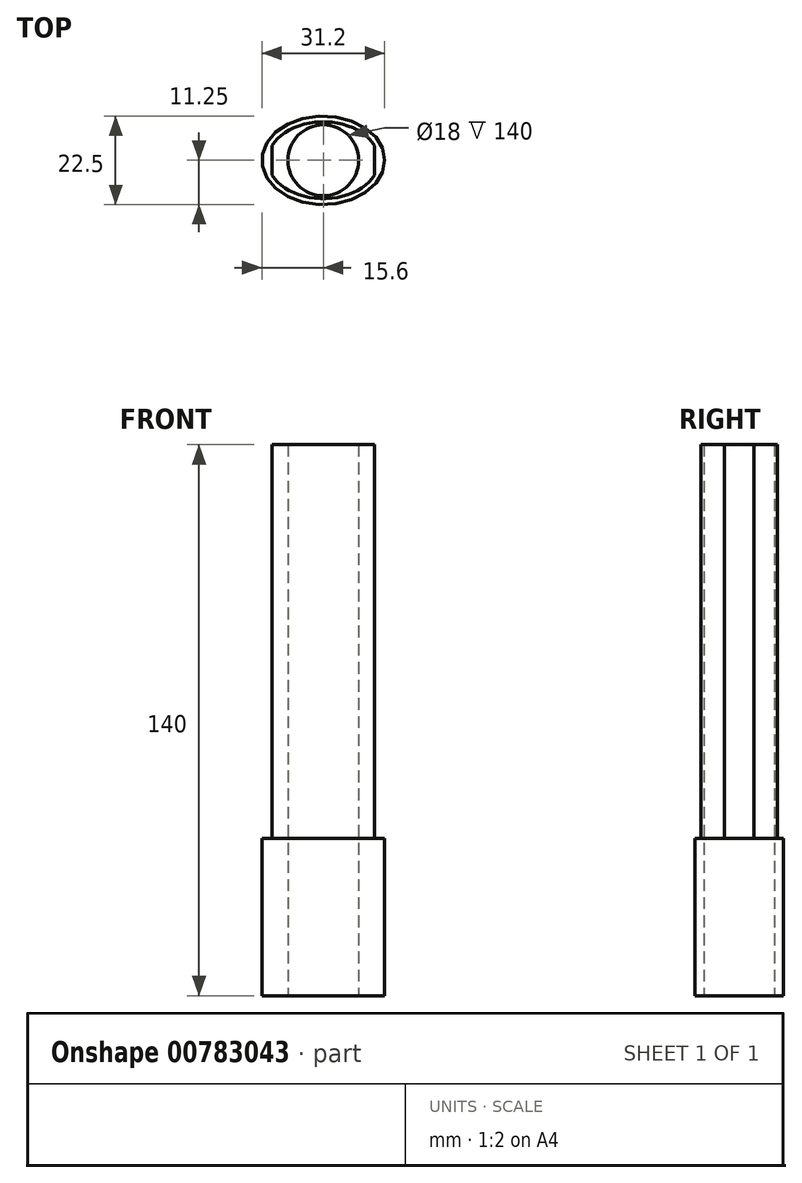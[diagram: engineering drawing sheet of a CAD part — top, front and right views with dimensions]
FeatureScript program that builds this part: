
annotation { "Feature Type Name" : "Feature", "Feature Type Description" : "" }
export const myFeature = defineFeature(function(context is Context, id is Id, definition is map)
    precondition{}
    {
        {
            var Q0;
            Q0=qCreatedBy(makeId("Top.planeOp"),FACE);
            var sketch = newSketch(context, id + "F0", { "sketchPlane" : qUnion([Q0])});
            skEllipse(sketch, "E0", {"center": v(0, 0) * mm, "majorRadius": 15.6 * mm, "minorRadius": 11.25 * mm, "majorAxis": v(1, 0)});
            skSolve(sketch);
        }
        {
            var Q0;
            Q0 = qSketchRegion(id + "F0", true);
            extrude(context, id + "F1", {"entities" : qUnion([Q0]), "depth" : 40 * mm, "offsetDistance" : 25.4 * mm});
        }
        {
            var Q0;
            Q0=makeQuery(id+"F1.opExtrude","CAP_FACE",FACE,{"disambiguationData":[OSD([sQuery(id+"F0.wireOp",EDGE,"E0")])],"isStart":false});
            var sketch = newSketch(context, id + "F2", { "sketchPlane" : qUnion([Q0])});
            skEllipticalArc(sketch, "E1", {});
            skLineSegment(sketch, "E2", {"start": v(13, 3.78) * mm, "end": v(13, -3.78) * mm});
            skLineSegment(sketch, "E3", {"start": v(-13, 3.78) * mm, "end": v(-13, -3.78) * mm});
            skEllipticalArc(sketch, "E4.trimOffspring", {});
            const initialGuessF2  = {"E1": [0, 0, 1, 0, 0.0141, 0.00975, 0.3976184106167527, 2.743974242973041], "E4.trimOffspring": [0, 0, 1, 0, 0.0141, 0.00975, 3.5392110642065457, 5.885566896562835]};
            skSetInitialGuess(sketch, initialGuessF2);
            skSolve(sketch);
        }
        {
            var Q0;
            Q0 = qSketchRegion(id + "F2", true);
            extrude(context, id + "F3", {"entities" : qUnion([Q0]), "operationType" : NewBodyOperationType.ADD, "depth" : 100 * mm, "offsetDistance" : 25 * mm});
        }
        {
            var Q0;
            Q0=sQuery(id+"F0.wireOp",VERTEX,"E0.center");
            var Q1;
            Q1=makeQuery(id+"F1.opExtrude","SWEPT_BODY",BODY,{"disambiguationData":[OSD([sQuery(id+"F0.wireOp",EDGE,"E0")])]});
            hole(context, id + "F4", {"style" : HoleStyle.SIMPLE, "endStyle" : HoleEndStyle.THROUGH, "oppositeDirection" : true, "holeDiameter" : 18 * mm, "majorDiameter" : 5 * mm, "isTappedThrough" : true, "tappedDepth" : 12 * mm, "tapClearance" : 3, "locations" : qUnion([Q0]), "scope" : qUnion([Q1])});
        }
    });
